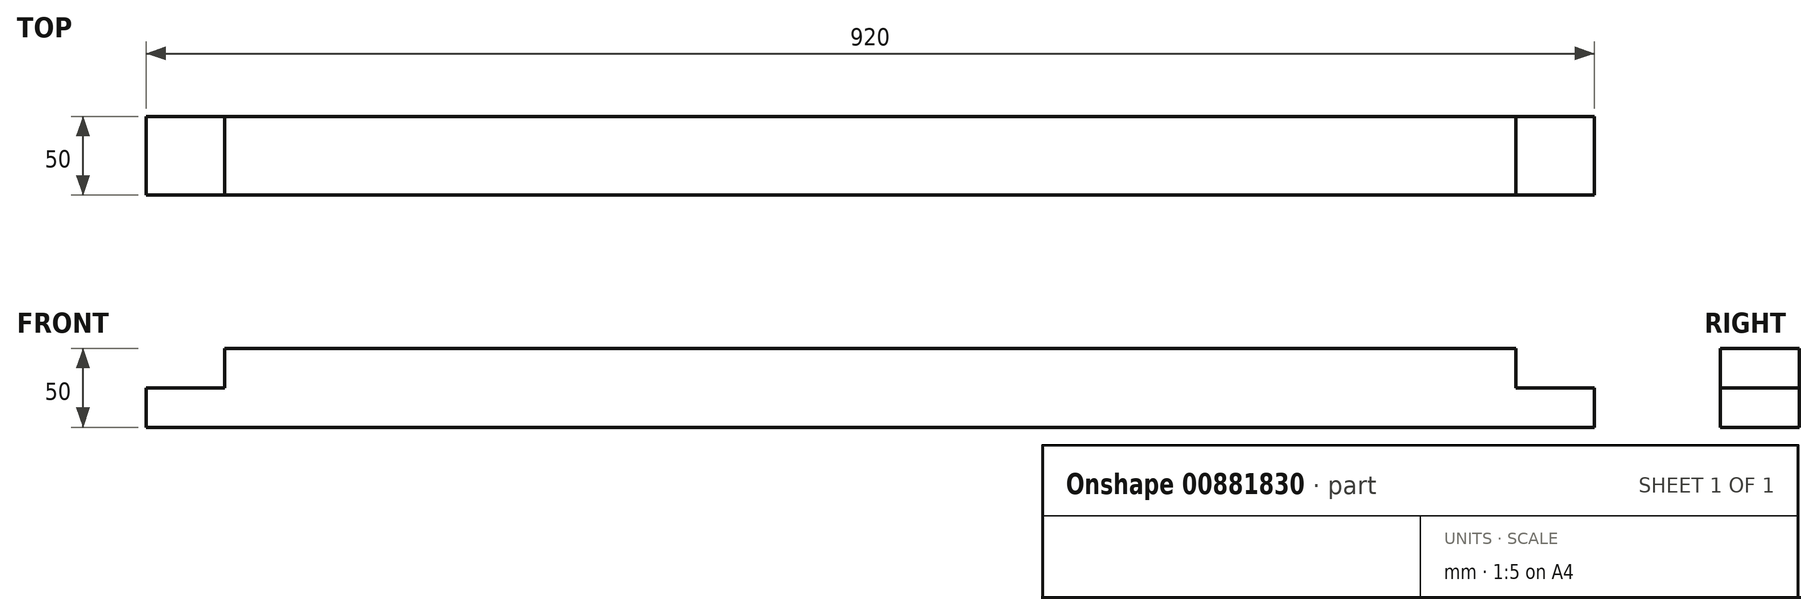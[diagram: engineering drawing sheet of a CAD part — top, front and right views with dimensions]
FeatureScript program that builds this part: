
annotation { "Feature Type Name" : "Feature", "Feature Type Description" : "" }
export const myFeature = defineFeature(function(context is Context, id is Id, definition is map)
    precondition{}
    {
        {
            var Q0;
            Q0=qCreatedBy(makeId("Front.planeOp"),FACE);
            var sketch = newSketch(context, id + "F0", { "sketchPlane" : qUnion([Q0])});
            skLineSegment(sketch, "E0", {"start": v(-88.8, 24.7) * mm, "end": v(831.2, 24.7) * mm});
            skLineSegment(sketch, "E1", {"start": v(831.2, 49.7) * mm, "end": v(781.2, 49.7) * mm});
            skLineSegment(sketch, "E2", {"start": v(781.2, 49.7) * mm, "end": v(781.2, 74.7) * mm});
            skLineSegment(sketch, "E3", {"start": v(781.2, 74.7) * mm, "end": v(-38.8, 74.7) * mm});
            skLineSegment(sketch, "E4", {"start": v(831.2, 24.7) * mm, "end": v(831.2, 49.7) * mm});
            skLineSegment(sketch, "E5", {"start": v(-88.8, 49.7) * mm, "end": v(-88.8, 24.7) * mm});
            skLineSegment(sketch, "E6", {"start": v(-88.8, 49.7) * mm, "end": v(-38.8, 49.7) * mm});
            skLineSegment(sketch, "E7", {"start": v(-38.8, 49.7) * mm, "end": v(-38.8, 74.7) * mm});
            skSolve(sketch);
        }
        {
            var Q0;
            Q0 = qSketchRegion(id + "F0", true);
            extrude(context, id + "F1", {"entities" : qUnion([Q0]), "depth" : 50 * mm, "offsetDistance" : 25 * mm});
        }
    });
